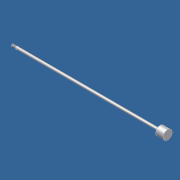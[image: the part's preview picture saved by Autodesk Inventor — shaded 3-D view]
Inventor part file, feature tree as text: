
AUTODESK INVENTOR PART (.ipt)
format: ipt  version: 2012 (Build 160160000, 160)  size: 135,168 bytes
history: native  units: in
note: dims shown in document units (in); Inventor stores cm internally (conversion verified against a paired STEP export)
features: other x112, sketch x3, revolve x2, thread x1, extrude x1
ambient origin geometry x8: Origin, YZ Plane, XZ Plane, XY Plane, X Axis, Y Axis, Z Axis, Center Point
bodies: Solid1 (feature_tree)
feature tree (119):
  revolve  "Revolution1"  Angle=360.0deg
  revolve  "Revolution2"  [1 undecoded]
  thread  "Thread1"  [1 undecoded]
  extrude  "Extrusion1"  [1 undecoded]
  other  "rod_cp_XY"
  other  "rod_cp_YZ"
  other  "rod_cp_ZX"
  other  "rod_cp_X"
  other  "rod_cp_Y"
  other  "rod_cp_Z"
  other  "rod_cp_Center"
  other  "to_rod_clevis_XY"
  other  "to_rod_clevis_YZ"
  other  "to_rod_clevis_ZX"
  other  "to_rod_clevis_X"
  other  "to_rod_clevis_Y"
  other  "to_rod_clevis_Z"
  other  "to_rod_clevis_Center"
  other  "rl2_XY"
  other  "rl2_YZ"
  other  "rl2_ZX"
  other  "rl2_X"
  other  "rl2_Y"
  other  "rl2_Z"
  other  "rl2_Center"
  other  "rl1_XY"
  other  "rl1_YZ"
  other  "rl1_ZX"
  other  "rl1_X"
  other  "rl1_Y"
  other  "rl1_Z"
  other  "rl1_Center"
  other  "thd1_XY"
  other  "thd1_YZ"
  other  "thd1_ZX"
  other  "thd1_X"
  other  "thd1_Y"
  other  "thd1_Z"
  other  "thd1_Center"
  other  "thd2_XY"
  other  "thd2_YZ"
  other  "thd2_ZX"
  other  "thd2_X"
  other  "thd2_Y"
  other  "thd2_Z"
  other  "thd2_Center"
  other  "dia1_XY"
  other  "dia1_YZ"
  other  "dia1_ZX"
  other  "dia1_X"
  other  "dia1_Y"
  other  "dia1_Z"
  other  "dia1_Center"
  other  "dia2_XY"
  other  "dia2_YZ"
  other  "dia2_ZX"
  other  "dia2_X"
  other  "dia2_Y"
  other  "dia2_Z"
  other  "dia2_Center"
  other  "wf1_XY"
  other  "wf1_YZ"
  other  "wf1_ZX"
  other  "wf1_X"
  other  "wf1_Y"
  other  "wf1_Z"
  other  "wf1_Center"
  other  "wf2_XY"
  other  "wf2_YZ"
  other  "wf2_ZX"
  other  "wf2_X"
  other  "wf2_Y"
  other  "wf2_Z"
  other  "wf2_Center"
  other  "hh1_XY"
  other  "hh1_YZ"
  other  "hh1_ZX"
  other  "hh1_X"
  other  "hh1_Y"
  other  "hh1_Z"
  other  "hh1_Center"
  other  "hh2_XY"
  other  "hh2_YZ"
  other  "hh2_ZX"
  other  "hh2_X"
  other  "hh2_Y"
  other  "hh2_Z"
  other  "hh2_Center"
  other  "dia12_XY"
  other  "dia12_YZ"
  other  "dia12_ZX"
  other  "dia12_X"
  other  "dia12_Y"
  other  "dia12_Z"
  other  "dia12_Center"
  other  "dia22_XY"
  other  "dia22_YZ"
  other  "dia22_ZX"
  other  "dia22_X"
  other  "dia22_Y"
  other  "dia22_Z"
  other  "dia22_Center"
  other  "wfw1_XY"
  other  "wfw1_YZ"
  other  "wfw1_ZX"
  other  "wfw1_X"
  other  "wfw1_Y"
  other  "wfw1_Z"
  other  "wfw1_Center"
  other  "wfw2_XY"
  other  "wfw2_YZ"
  other  "wfw2_ZX"
  other  "wfw2_X"
  other  "wfw2_Y"
  other  "wfw2_Z"
  other  "wfw2_Center"
  sketch  "Sketch_1"  dims[d0=360.0deg d1=360.0deg]
  sketch  "Sketch_3"  dims[d2=0.5in d3=0.0in d4=0.125in d5=0.0in]
  sketch  "Sketch_10"
note: 3 required parameter values undecoded (feature->parameter linkage not recoverable at this tier; creation-order binding heuristic only, values carry confidence <= 0.55)